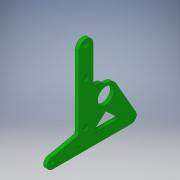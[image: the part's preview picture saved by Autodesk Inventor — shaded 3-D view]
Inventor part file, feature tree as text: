
AUTODESK INVENTOR PART (.ipt)
format: ipt  version: 2018 (Build 220112000, 112)  size: 186,880 bytes
history: native  units: in
note: dims shown in document units (in); Inventor stores cm internally (conversion verified against a paired STEP export)
features: extrude x2, chamfer x1, sketch x1, projected_geometry x1
ambient origin geometry x8: Origin, YZ Plane, XZ Plane, XY Plane, X Axis, Y Axis, Z Axis, Center Point
bodies: Solid1 (feature_tree)
feature tree (5):
  extrude  "Extrusion1"  Depth=5.0in
  chamfer  "Chamfer1"  Distance=0.5in
  extrude  "Extrusion2"  Depth=1.0in
  sketch  "Sketch2"  dims[d0=0.196in d1=5.0in d3=0.5in d13=1.0in d14=0.375in d18=0.25in d19=0.0in d20=0.375in d30=0.125in d31=0.125in d32=45.0deg d33=1.125in d34=1.0in d35=1.75in d37=3.0in d38=2.725in d39=0.875in d40=0.375in d42=0.4566in d45=0.264in d46=0.467in d47=0.264in d52=1.763in d53=1.7631in d54=1.9739in d55=2.345in d56=0.25in d57=0.0in d58=0.25in d60=2.47in d62=0.625in d63=0.375in d64=0.375in d65=1.0in d66=0.0in d67=1.0in]
  projected_geometry  "Projected Loop1"
